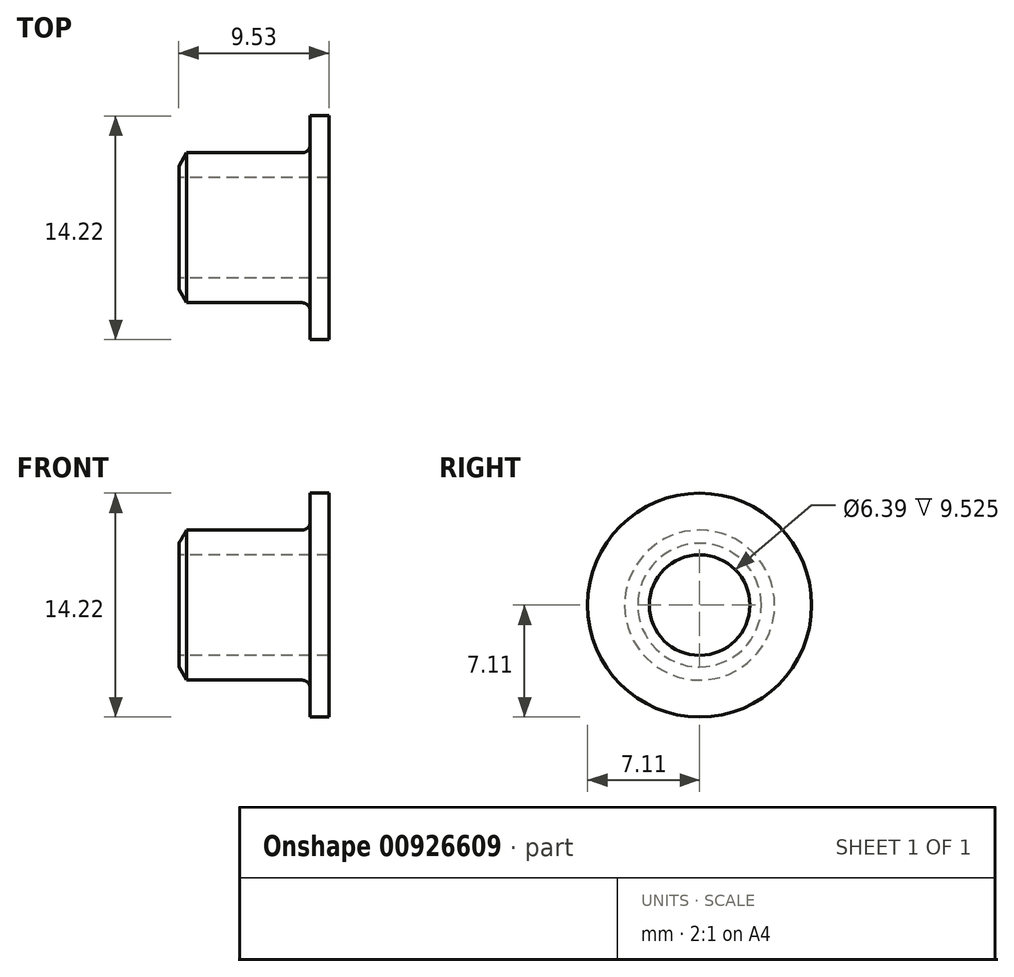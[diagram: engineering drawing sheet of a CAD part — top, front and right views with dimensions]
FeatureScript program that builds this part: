
annotation { "Feature Type Name" : "Feature", "Feature Type Description" : "" }
export const myFeature = defineFeature(function(context is Context, id is Id, definition is map)
    precondition{}
    {
        {
            var Q0;
            Q0=qCreatedBy(makeId("Front.planeOp"),FACE);
            var sketch = newSketch(context, id + "F0", { "sketchPlane" : qUnion([Q0])});
            skLineSegment(sketch, "E0", {"start": v(-9.53, 3.2) * mm, "end": v(0, 3.2) * mm});
            skLineSegment(sketch, "E1", {"start": v(0, 3.2) * mm, "end": v(0, 7.11) * mm});
            skLineSegment(sketch, "E2", {"start": v(0, 7.11) * mm, "end": v(-1.2, 7.11) * mm});
            skLineSegment(sketch, "E3", {"start": v(-1.2, 7.11) * mm, "end": v(-1.2, 5.27) * mm});
            skLineSegment(sketch, "E4", {"start": v(-1.7, 4.76) * mm, "end": v(-9.04, 4.76) * mm});
            skLineSegment(sketch, "E5", {"start": v(-9.04, 4.76) * mm, "end": v(-9.53, 3.93) * mm});
            skLineSegment(sketch, "E6", {"start": v(-9.53, 3.93) * mm, "end": v(-9.53, 3.2) * mm});
            skPoint(sketch, "E7.visualSharp", {"position": v(-1.2, 4.76) * mm});
            skArc(sketch, "E7.filletArc", {"start": v(-1.7, 4.76) * mm, "mid": v(-1.34, 4.91) * mm, "end": v(-1.2, 5.27) * mm});
            skLineSegment(sketch, "E8", {"start": v(-13.49, 0) * mm, "end": v(6.08, 0) * mm});
            skSolve(sketch);
        }
        {
            var Q0;
            Q0=makeQuery(id+"F0.imprint","IMPRINT",FACE,{"disambiguationData":[TD([[makeQuery(id+"F0.imprint","IMPRINT",EDGE,{"derivedFrom":sQuery(id+"F0.wireOp",EDGE,"E0")}),1.0]])]});
            var Q1;
            Q1=sQuery(id+"F0.wireOp",EDGE,"E8");
            revolve(context, id + "F1", {"surfaceOperationType" : NewSurfaceOperationType.NEW, "entities" : qUnion([Q0]), "axis" : qUnion([Q1]), "revolveType" : RevolveType.FULL});
        }
    });
